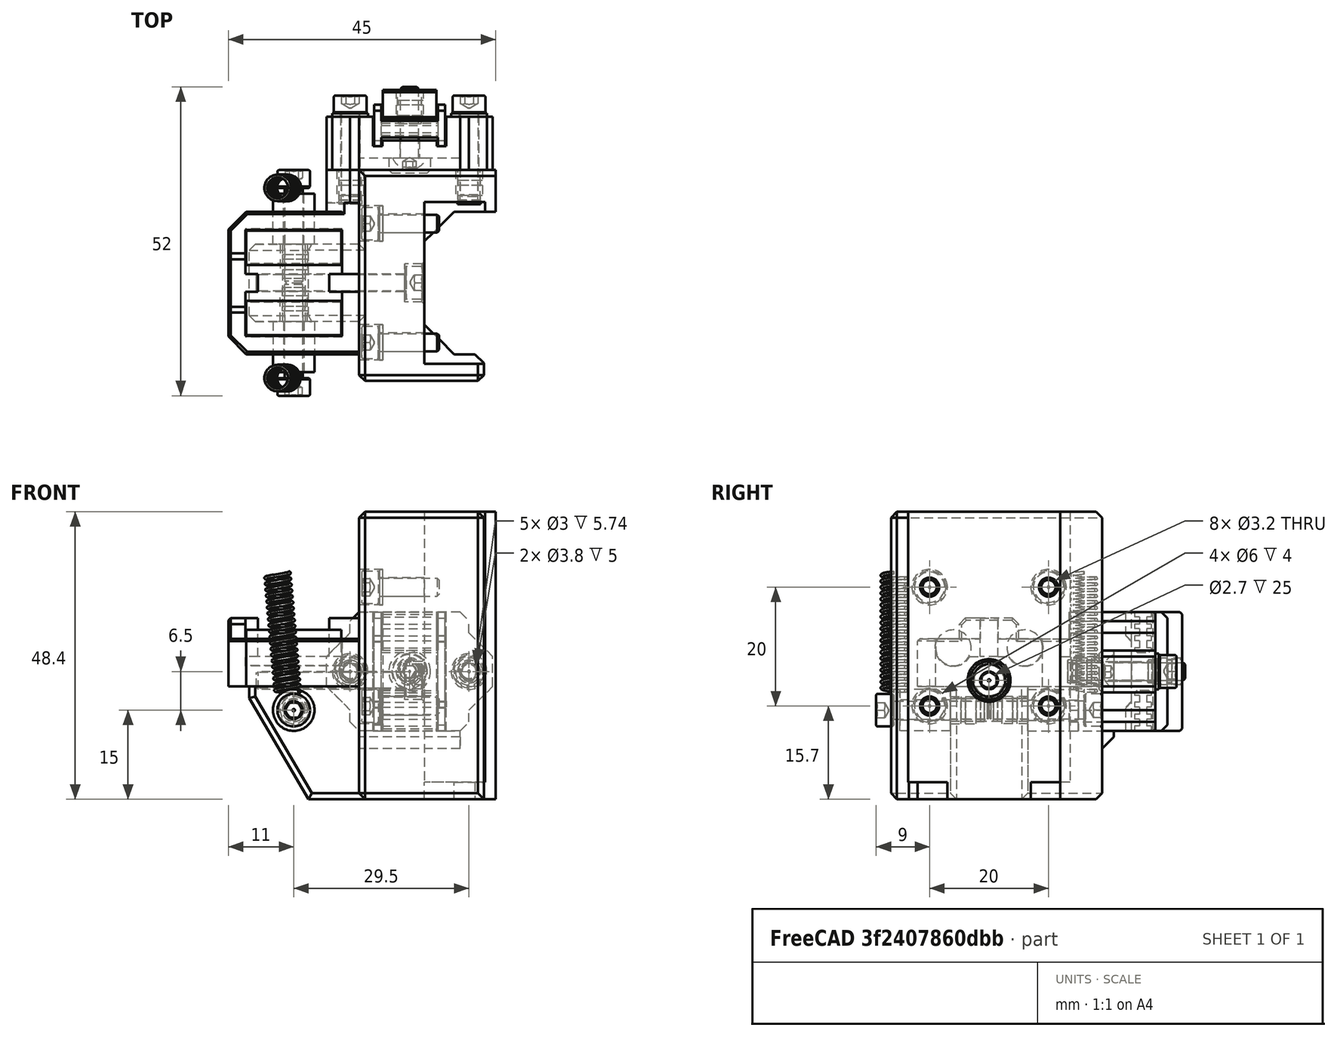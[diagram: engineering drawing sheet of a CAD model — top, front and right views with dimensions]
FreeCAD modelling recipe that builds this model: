
FCSTD DOCUMENT  (FreeCAD 0.19R24291 (Git))
Label: z-block-mount-right-assembly
License: Other
LicenseURL: GPL3
objects: Part::FeaturePython×22, Part::Feature×10, PartDesign::CoordinateSystem×1, App::Part×1
note: 33 computed .brp shape members not serialized (recipe doc carries the construction recipe); baked Part::Feature solids carry a one-line shape summary decoded from their .brp

FEATURE [Part::Feature] Cut028006004005011004003001010002002004007  label="bed-spring-bottom-spacer002"
  Placement = pos=(-22,-6.5,12) rot=(1,0,0;1.5708rad)
  shape: bbox 7 x 8.5 x 7 mm, 4 faces (baked)
FEATURE [Part::Feature] Cut028006004005011004003001010002002004008  label="bed-spring-bottom-spacer003"
  Placement = pos=(-22,6.5,12) rot=(-1,0,0;1.5708rad)
  shape: bbox 7 x 8.5 x 7 mm, 4 faces (baked)
FEATURE [Part::Feature] Chamfer004013007011015006002002  label="z-belt-block-mount001"
  Placement = pos=(-5,-12.5,0) rot=(0,0,1;0rad)
  shape: bbox 28 x 9 x 20 mm, 47 faces (baked)
FEATURE [Part::Feature] Cut028006004005011004003001010002002004009  label="z-belt-mounter-middle001"
  Placement = pos=(-5,-14,0) rot=(0,0,1;0rad)
  shape: bbox 12 x 7 x 20 mm, 80 faces (baked)
FEATURE [Part::Feature] Cut028006004005011004003001010002002004010  label="z-belt-mounter-clamp-nut001"
  Placement = pos=(-2.5,36,18.5) rot=(-1,0,0;1.5708rad)
  shape: bbox 9 x 5 x 20 mm, 11 faces (baked)
FEATURE [Part::Feature] Cylinder032002  label="6x16-dowel-pin002"
  Placement = pos=(-14,6,22.5) rot=(0.57735,-0.57735,-0.57735;2.0944rad)
  shape: bbox 16 x 6 x 6 mm, 3 faces (baked)
FEATURE [Part::Feature] Cylinder032003  label="6x16-dowel-pin003"
  Placement = pos=(-14,-6,22.5) rot=(0.57735,-0.57735,-0.57735;2.0944rad)
  shape: bbox 16 x 6 x 6 mm, 3 faces (baked)
FEATURE [Part::FeaturePython] Washer006  label="M3-Washer"  # Fasteners workbench fastener (typed FeaturePython)
  Placement = pos=(-7,10,12.7) rot=(0,-1,0;1.5708rad)
  diameter = 4
  invert = true
  matchOuter = true
  offset = 0
  type = 5
FEATURE [Part::FeaturePython] Washer007  label="M3-Washer020"  # Fasteners workbench fastener (typed FeaturePython)
  Placement = pos=(-7,10,32.7) rot=(0,-1,0;1.5708rad)
  diameter = 4
  invert = true
  matchOuter = true
  offset = 0
  type = 5
FEATURE [Part::FeaturePython] Washer008  label="M3-Washer021"  # Fasteners workbench fastener (typed FeaturePython)
  Placement = pos=(-7,-10,32.7) rot=(0,-1,0;1.5708rad)
  diameter = 4
  invert = true
  matchOuter = true
  offset = 0
  type = 5
FEATURE [Part::FeaturePython] Washer009  label="M3-Washer022"  # Fasteners workbench fastener (typed FeaturePython)
  Placement = pos=(-7,-10,12.7) rot=(0,-1,0;1.5708rad)
  diameter = 4
  invert = true
  matchOuter = true
  offset = 0
  type = 5
FEATURE [Part::FeaturePython] Screw009  label="M3x10-Screw"  # Fasteners workbench fastener (typed FeaturePython)
  Placement = pos=(-7.55,10,12.7) rot=(0,-1,0;1.5708rad)
  baseObject = -> Washer006 [Edge1]
  diameter = 4
  invert = false
  length = 3
  lengthCustom = 10
  matchOuter = true
  offset = 0
  thread = false
  type = 34
FEATURE [Part::FeaturePython] Screw010  label="M3x10-Screw004"  # Fasteners workbench fastener (typed FeaturePython)
  Placement = pos=(-7.55,10,32.7) rot=(0,-1,0;1.5708rad)
  baseObject = -> Washer007 [Edge1]
  diameter = 4
  invert = false
  length = 3
  lengthCustom = 10
  matchOuter = true
  offset = 0
  thread = false
  type = 34
FEATURE [Part::FeaturePython] Screw011  label="M3x10-Screw005"  # Fasteners workbench fastener (typed FeaturePython)
  Placement = pos=(-7.55,-10,32.7) rot=(0,-1,0;1.5708rad)
  baseObject = -> Washer008 [Edge1]
  diameter = 4
  invert = false
  length = 3
  lengthCustom = 10
  matchOuter = true
  offset = 0
  thread = false
  type = 34
FEATURE [Part::FeaturePython] Screw012  label="M3x10-Screw006"  # Fasteners workbench fastener (typed FeaturePython)
  Placement = pos=(-7.55,-10,12.7) rot=(0,-1,0;1.5708rad)
  baseObject = -> Washer009 [Edge1]
  diameter = 4
  invert = false
  length = 3
  lengthCustom = 10
  matchOuter = true
  offset = 0
  thread = false
  type = 34
FEATURE [Part::FeaturePython] HeatSet006  label="M3x4-HeatSet005"  # WARN: FeaturePython — macro-defined, semantics opaque (R4)
  Placement = pos=(-22,-6.5,12) rot=(1,0,0;1.5708rad)
  baseObject = -> Cut028006004005011004003001010002002004007 [Edge3]
  diameter = 2
  invert = false
  offset = 0
FEATURE [Part::FeaturePython] HeatSet007  label="M3x4-HeatSet006"  # WARN: FeaturePython — macro-defined, semantics opaque (R4)
  Placement = pos=(7.5,19,18.5) rot=(-1,0,0;1.5708rad)
  diameter = 2
  invert = true
  offset = 0
FEATURE [Part::FeaturePython] HeatSet008  label="M3x4-HeatSet007"  # WARN: FeaturePython — macro-defined, semantics opaque (R4)
  Placement = pos=(-12.5,19,18.5) rot=(-1,0,0;1.5708rad)
  diameter = 2
  invert = true
  offset = 0
FEATURE [Part::FeaturePython] HeatSet009  label="M3x4-HeatSet008"  # WARN: FeaturePython — macro-defined, semantics opaque (R4)
  Placement = pos=(-22,6.5,12) rot=(-1,0,0;1.5708rad)
  diameter = 2
  invert = false
  offset = 0
FEATURE [Part::FeaturePython] HeatSet010  label="M3x4-HeatSet009"  # WARN: FeaturePython — macro-defined, semantics opaque (R4)
  Placement = pos=(-22,-6.5,12) rot=(1,0,0;1.5708rad)
  diameter = 2
  invert = true
  offset = 0
FEATURE [Part::FeaturePython] HeatSet011  label="M3x4-HeatSet010"  # WARN: FeaturePython — macro-defined, semantics opaque (R4)
  Placement = pos=(-2.5,32.5,18.5) rot=(-1,0,0;1.5708rad)
  baseObject = -> Cut028006004005011004003001010002002004010 [Edge21]
  diameter = 2
  invert = false
  offset = 0
FEATURE [Part::FeaturePython] Screw013  label="M3x12-Screw001"  # Fasteners workbench fastener (typed FeaturePython)
  Placement = pos=(-2.5,21,18.5) rot=(1,0,0;1.5708rad)
  baseObject = -> Chamfer004013007011015006002002 [Edge132]
  diameter = 1
  invert = false
  length = 3
  lengthCustom = 12
  matchOuter = true
  offset = 0
  thread = false
  type = 40
FEATURE [Part::FeaturePython] Washer010  label="M3-Washer018"  # Fasteners workbench fastener (typed FeaturePython)
  Placement = pos=(7.5,28,18.5) rot=(-1,0,0;1.5708rad)
  baseObject = -> Chamfer004013007011015006002002 [Edge96]
  diameter = 4
  invert = true
  matchOuter = true
  offset = 0
  type = 5
FEATURE [Part::FeaturePython] Washer011  label="M3-Washer019"  # Fasteners workbench fastener (typed FeaturePython)
  Placement = pos=(-12.5,28,18.5) rot=(-1,0,0;1.5708rad)
  baseObject = -> Chamfer004013007011015006002002 [Edge15]
  diameter = 4
  invert = true
  matchOuter = true
  offset = 0
  type = 5
FEATURE [Part::FeaturePython] Screw014  label="M3x14-Screw002"  # Fasteners workbench fastener (typed FeaturePython)
  Placement = pos=(7.5,28.55,18.5) rot=(-1,0,0;1.5708rad)
  baseObject = -> Washer010 [Edge1]
  diameter = 4
  invert = false
  length = 5
  lengthCustom = 14
  matchOuter = true
  offset = 0
  thread = false
  type = 34
FEATURE [Part::FeaturePython] Screw015  label="M3x14-Screw003"  # Fasteners workbench fastener (typed FeaturePython)
  Placement = pos=(-12.5,28.55,18.5) rot=(-1,0,0;1.5708rad)
  baseObject = -> Washer011 [Edge1]
  diameter = 4
  invert = false
  length = 5
  lengthCustom = 14
  matchOuter = true
  offset = 0
  thread = false
  type = 34
FEATURE [Part::FeaturePython] Screw016  label="M3x16-Screw005"  # Fasteners workbench fastener (typed FeaturePython)
  Placement = pos=(-22,16,12) rot=(-1,0,0;1.5708rad)
  baseObject = -> Cut028006004005011004003001010002002004008 [Edge4]
  diameter = 4
  invert = false
  length = 6
  lengthCustom = 16
  matchOuter = true
  offset = 1
  thread = false
  type = 34
FEATURE [Part::FeaturePython] Screw017  label="M3x16-Screw006"  # Fasteners workbench fastener (typed FeaturePython)
  Placement = pos=(-22,-16,12) rot=(1,0,0;1.5708rad)
  baseObject = -> Cut028006004005011004003001010002002004007 [Edge4]
  diameter = 4
  invert = false
  length = 6
  lengthCustom = 16
  matchOuter = true
  offset = 1
  thread = false
  type = 34
FEATURE [Part::Feature] Body001001005  label="hook-spring-005"
  Placement = pos=(-23,-16,15) rot=(0,0,1;0rad)
  shape: bbox 6.31 x 4.635 x 20.83 mm, 22 faces (baked)
FEATURE [Part::Feature] Body001001006  label="hook-spring-006"
  Placement = pos=(-23,16,15) rot=(0,0,1;0rad)
  shape: bbox 6.31 x 4.635 x 20.83 mm, 22 faces (baked)
FEATURE [Part::FeaturePython] Screw018  label="M3x25-Screw"  # Fasteners workbench fastener (typed FeaturePython)
  Placement = pos=(-3.3,0,17) rot=(0,1,0;1.5708rad)
  diameter = 4
  invert = false
  length = 8
  lengthCustom = 25
  matchOuter = true
  offset = 0
  thread = false
  type = 34
FEATURE [PartDesign::CoordinateSystem] LCS_z_rail_block_mount_x_slider  label="LCS_z-rail-block-mount-x-slider"
  AttacherType = Attacher::AttachEngine3D
FEATURE [Part::Feature] Part__Mirroring002001001  label="z-rail-block-mount-right-with-limiter"
  shape: bbox 45 x 37.5 x 48.4 mm, 119 faces (baked)
FEATURE [App::Part] Part001  label="z-rail-block-mount-x-slider"
  Group = -> [Cylinder032002,Cylinder032003,Cut028006004005011004003001010002002004010,Cut028006004005011004003001010002002004009,Chamfer004013007011015006002002,Cut028006004005011004003001010002002004008,Cut028006004005011004003001010002002004007,Body001001005,Body001001006,Washer006,Washer007,Washer008,Washer009,Screw009,Screw010,Screw011,Screw012,HeatSet006,HeatSet007,HeatSet008,HeatSet009,HeatSet010,+11 more]
  Origin = -> Origin001
